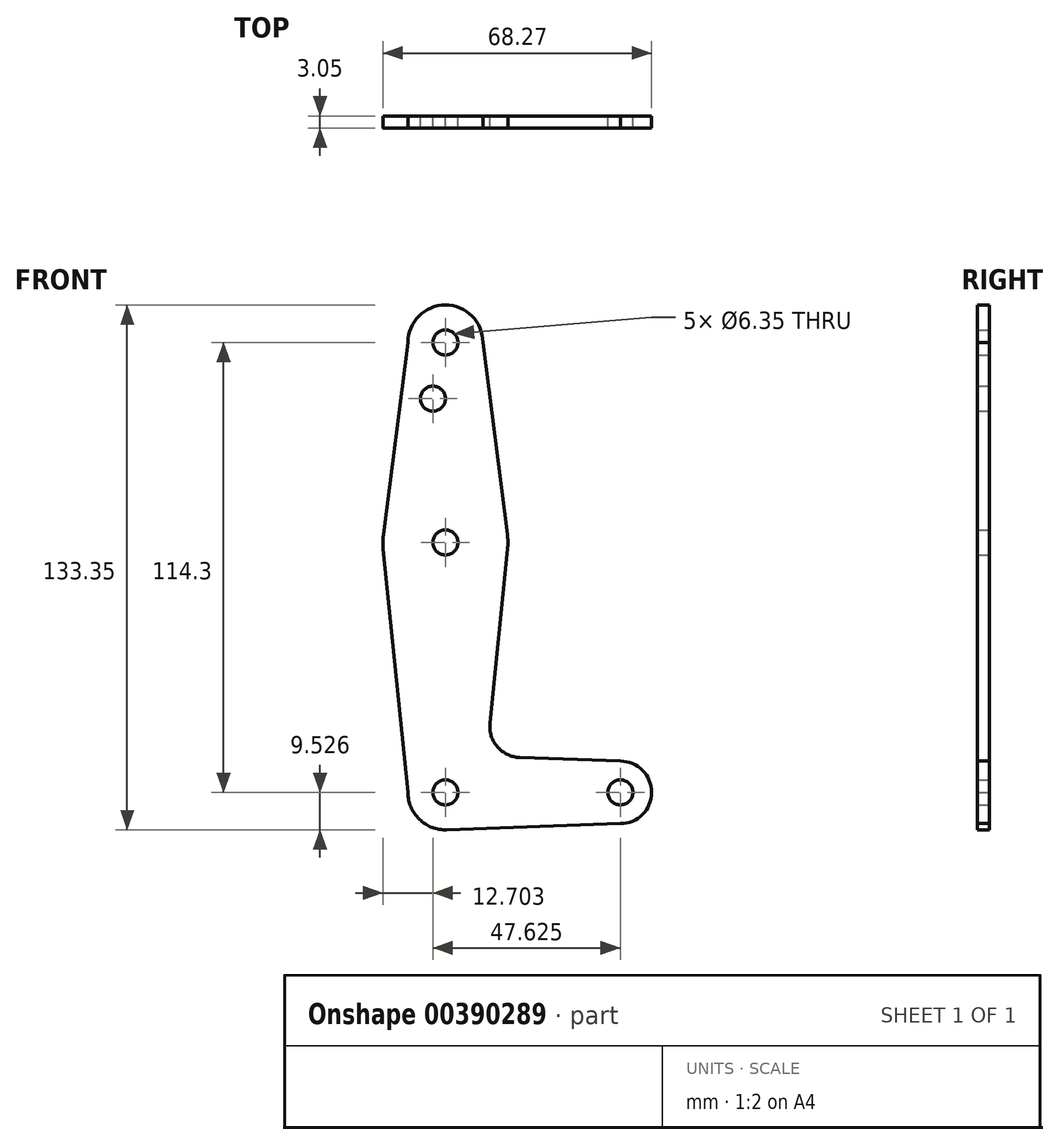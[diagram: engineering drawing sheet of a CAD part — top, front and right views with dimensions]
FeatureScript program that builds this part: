
annotation { "Feature Type Name" : "Feature", "Feature Type Description" : "" }
export const myFeature = defineFeature(function(context is Context, id is Id, definition is map)
    precondition{}
    {
        {
            var Q0;
            Q0=qCreatedBy(makeId("Front.planeOp"),FACE);
            var sketch = newSketch(context, id + "F0", { "sketchPlane" : qUnion([Q0])});
            skLineSegment(sketch, "E0", {"start": v(-40.8, 66.9) * mm, "end": v(-40.8, -47.4) * mm, "construction": true});
            skLineSegment(sketch, "E1", {"start": v(-40.8, -47.4) * mm, "end": v(3.65, -47.4) * mm, "construction": true});
            skCircle(sketch, "E2", {"center": v(-40.8, 66.9) * mm, "radius": 9.53 * mm});
            skCircle(sketch, "E3", {"center": v(-40.8, 16.1) * mm, "radius": 15.88 * mm});
            skCircle(sketch, "E4", {"center": v(-40.8, -47.4) * mm, "radius": 9.53 * mm});
            skCircle(sketch, "E5", {"center": v(3.65, -47.4) * mm, "radius": 7.94 * mm});
            skPoint(sketch, "E6", {"position": v(-50.33, 66.9) * mm});
            skPoint(sketch, "E7", {"position": v(-31.28, 66.9) * mm});
            skLineSegment(sketch, "E8", {"start": v(-50.33, 66.9) * mm, "end": v(-56.55, 18.11) * mm});
            skLineSegment(sketch, "E9", {"start": v(-31.28, 66.9) * mm, "end": v(-25.05, 18.11) * mm});
            skPoint(sketch, "E10", {"position": v(-31.28, -47.4) * mm});
            skPoint(sketch, "E11", {"position": v(-50.33, -47.4) * mm});
            skLineSegment(sketch, "E12", {"start": v(-50.33, -47.4) * mm, "end": v(-56.6, 14.5) * mm});
            skLineSegment(sketch, "E13", {"start": v(-29.5, -29.8) * mm, "end": v(-25, 14.5) * mm});
            skPoint(sketch, "E14", {"position": v(3.65, -39.46) * mm});
            skPoint(sketch, "E15", {"position": v(3.65, -55.33) * mm});
            skLineSegment(sketch, "E16", {"start": v(3.65, -39.46) * mm, "end": v(-21.87, -38.54) * mm});
            skLineSegment(sketch, "E17", {"start": v(3.65, -55.33) * mm, "end": v(-40.46, -56.91) * mm});
            skCircle(sketch, "E18", {"center": v(-40.8, 66.9) * mm, "radius": 3.18 * mm});
            skCircle(sketch, "E19", {"center": v(-40.8, 16.1) * mm, "radius": 3.18 * mm});
            skCircle(sketch, "E20", {"center": v(-40.8, -47.4) * mm, "radius": 3.18 * mm});
            skCircle(sketch, "E21", {"center": v(3.65, -47.4) * mm, "radius": 3.18 * mm});
            skCircle(sketch, "E22", {"center": v(-43.98, 52.63) * mm, "radius": 3.18 * mm});
            skArc(sketch, "E23.filletArc", {"start": v(-29.5, -29.8) * mm, "mid": v(-27.58, -35.82) * mm, "end": v(-21.87, -38.54) * mm});
            skSolve(sketch);
        }
        {
            var Q0;
            Q0 = qSketchRegion(id + "F0", true);
            extrude(context, id + "F1", {"entities" : qUnion([Q0]), "depth" : 3.05 * mm});
        }
    });
